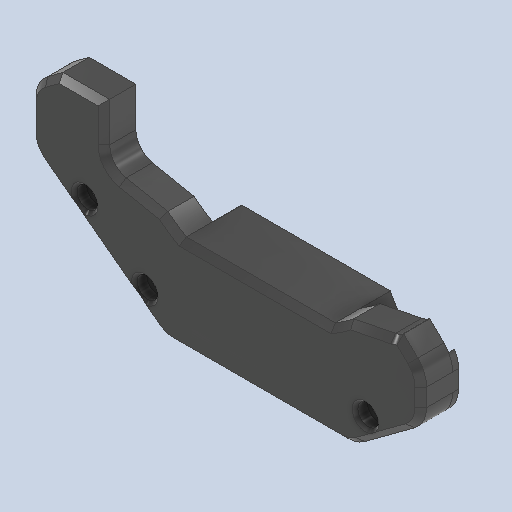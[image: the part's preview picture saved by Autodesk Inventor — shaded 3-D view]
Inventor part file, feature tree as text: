
AUTODESK INVENTOR PART (.ipt)
format: ipt  version: 2023.4 (Build 274418000, 418)  size: 692,224 bytes
history: native  units: mm
features: extrude x9, sketch x9, chamfer x5, projected_geometry x5, thicken_offset x2
ambient origin geometry x8: Origin, YZ Plane, XZ Plane, XY Plane, X Axis, Y Axis, Z Axis, Center Point
bodies: Solid1 (feature_tree)
feature tree (30):
  extrude  "Extrusion1"  Depth=10.0mm TaperAngle=0.0deg
  extrude  "Extrusion2"  Depth=6.0mm TaperAngle=0.0deg
  extrude  "Extrusion3"  Depth=4.3mm
  extrude  "Extrusion4"  Depth=4.3mm
  extrude  "Extrusion5"  Depth=10.0mm
  extrude  "Extrusion6"  Depth=7.2mm
  extrude  "Extrusion7"  Depth=3.3mm TaperAngle=0.0deg
  extrude  "Extrusion8"  Depth=10.0mm
  extrude  "Extrusion9"  Depth=2.0mm TaperAngle=45.0deg
  thicken_offset  "Thicken1"
  chamfer  "Chamfer1"  Distance=2.0mm Angle=45.0deg
  chamfer  "Chamfer2"  Distance=2.0mm Angle=45.0deg
  chamfer  "Chamfer3"  Distance=2.0mm Angle=45.0deg
  chamfer  "Chamfer4"  Distance=0.1mm
  thicken_offset  "Thicken2"
  chamfer  "Chamfer5"  Distance=0.1mm
  sketch  "Sketch1"  dims[d0=10.0mm d1=0.0mm d2=20.0mm d3=0.0mm]
  sketch  "Sketch2"  dims[d4=12.0mm d5=0.0mm d6=6.0mm d7=0.0mm]
  sketch  "Sketch5"  dims[d8=6.0mm d9=0.0mm d10=4.3mm]
  sketch  "Sketch6"  dims[d11=4.3mm d12=4.3mm]
  projected_geometry  "Projected Loop1"
  sketch  "Sketch7"  dims[d13=10.0mm d14=0.0mm d15=7.2mm]
  sketch  "Sketch8"  dims[d16=7.2mm d17=7.2mm]
  sketch  "Sketch9"  dims[d18=1.0mm d19=0.0mm d20=3.3mm d21=0.0mm]
  projected_geometry  "Projected Loop2"
  sketch  "Sketch10"  dims[d22=10.0mm d23=0.0mm d24=0.1mm]
  projected_geometry  "Projected Loop3"
  projected_geometry  "Projected Loop4"
  projected_geometry  "Projected Loop5"
  sketch  "Sketch11"  dims[d25=0.1mm d26=2.0mm d27=2.0mm d28=45.0deg d29=2.0mm d30=2.0mm d31=45.0deg d32=2.0mm d33=2.0mm d34=45.0deg d35=2.0mm d36=2.0mm d37=45.0deg d38=0.1mm d39=0.1mm d40=1.0mm d41=2.0mm d42=45.0deg]
